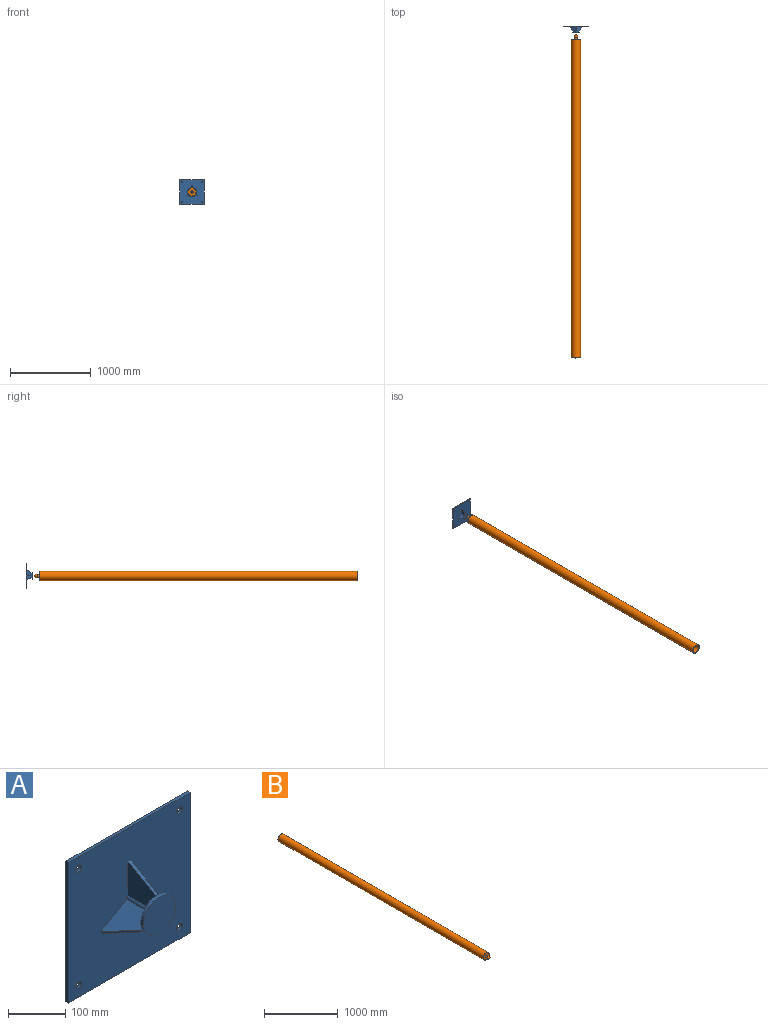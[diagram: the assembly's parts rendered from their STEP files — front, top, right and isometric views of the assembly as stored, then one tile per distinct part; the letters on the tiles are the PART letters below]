
ASSEMBLY  parts=2 mates=2
PART A: 30 faces, bbox 300x80.6x300 mm
  f0: plane 5.63x3.41mm, normal (0,-1,0), area 1.2mm2, adj f2,f23,f24,f27
  f1: plane 6.35x0.27mm, normal (0,-1,0), area 1.2mm2, adj f7,f19,f20,f27
  f2: plane 67.95x64.65mm, normal (0.5,0,0.87), area 3691.5mm2, adj f0,f16,f18,f24,f25
  f3: plane 5.63x3.41mm, normal (0,-1,0), area 1.2mm2, adj f5,f21,f22,f27
  f4: cylinder r=6.35mm len=67.95mm, axis (0,1,0), area 451.8mm2, adj f5,f16,f23,f29
  f5: plane 67.95x64.65mm, normal (0.5,0,-0.87), area 3691.5mm2, adj f3,f4,f16,f22,f29
  f6: cylinder r=6.35mm len=67.95mm, axis (0,1,0), area 451.8mm2, adj f7,f16,f21,f26
  f7: plane 74.65x67.95mm, normal (-1,0,0), area 3691.5mm2, adj f1,f6,f16,f20,f26
  f8: plane 300x6.35mm, normal (0,0,1), area 1905mm2, adj f9,f15,f16,f17
  f9: plane 300x6.35mm, normal (-1,0,0), area 1905mm2, adj f8,f10,f16,f17
  f10: plane 300x6.35mm, normal (0,0,-1), area 1905mm2, adj f9,f15,f16,f17
  f11: cylinder r=7.14mm len=14.29mm, axis (0,1,0), area 285mm2, adj f16,f17
  f12: cylinder r=7.14mm len=14.29mm, axis (0,1,0), area 285mm2, adj f16,f17
  f13: cylinder r=7.14mm len=14.29mm, axis (0,1,0), area 285mm2, adj f16,f17
  f14: cylinder r=7.14mm len=14.29mm, axis (0,1,0), area 285mm2, adj f16,f17
  f15: plane 300x6.35mm, normal (1,0,0), area 1905mm2, adj f8,f10,f16,f17
  f16: plane 300x300mm, normal (0,-1,0), area 87820.9mm2, adj f2,f4,f5,f6,f7,f8,f9,f10
  f17: plane 300x300mm, normal (0,1,0), area 89358.7mm2, adj f8,f9,f10,f11,f12,f13,f14,f15
  f18: cylinder r=6.35mm len=67.95mm, axis (0,1,0), area 451.8mm2, adj f2,f16,f19,f25
  f19: plane 74.65x67.95mm, normal (1,0,0), area 3691.5mm2, adj f1,f16,f18,f20,f25
  f20: plane 67.95x40.64mm, normal (0,-0.51,0.86), area 502.7mm2, adj f1,f7,f16,f19
  f21: plane 67.95x64.65mm, normal (-0.5,0,0.87), area 3691.5mm2, adj f3,f6,f16,f22,f26
  f22: plane 67.95x38.37mm, normal (-0.74,-0.51,-0.43), area 502.7mm2, adj f3,f5,f16,f21
  f23: plane 67.95x64.65mm, normal (-0.5,0,-0.87), area 3691.5mm2, adj f0,f4,f16,f24,f29
  f24: plane 67.95x38.37mm, normal (0.74,-0.51,-0.43), area 502.7mm2, adj f0,f2,f16,f23
  f25: plane 56.11x36.2mm, normal (0,1,0), area 1369.8mm2, adj f2,f18,f19,f27
  f26: plane 56.11x36.2mm, normal (0,1,0), area 1369.8mm2, adj f6,f7,f21,f27
  f27: cylinder r=39.37mm len=78.74mm, axis (0,1,0), area 1570.8mm2, adj f0,f1,f3,f25,f26,f28,f29
  f28: plane 78.74x78.74mm, normal (0,-1,0), area 4869.5mm2, adj f27
  f29: plane 64.79x33.87mm, normal (0,1,0), area 1369.8mm2, adj f4,f5,f23,f27
PART B: 7 faces, bbox 114.3x4011x114.3 mm
  f0: cylinder r=50.8mm len=3943.35mm, axis (0,1,0), area 1258661.4mm2, adj f2,f3
  f1: cylinder r=57.15mm len=3949.7mm, axis (0,1,0), area 1418274.2mm2, adj f2,f4
  f2: plane 114.3x114.3mm, normal (0,1,0), area 2153.5mm2, adj f0,f1
  f3: plane 101.6x101.6mm, normal (0,1,0), area 8107.3mm2, adj f0
  f4: plane 114.3x114.3mm, normal (0,-1,0), area 9754.1mm2, adj f1,f6
  f5: sphere r=20mm, area 4454.8mm2, adj f6
  f6: cylinder r=12.7mm len=25.82mm, axis (0,-1,0), area 2060.7mm2, adj f4,f5
PLACE A t=(-692.63,-15.51,310.29)mm fixed
PLACE B rot(axis=(-0.58,0,-0.81),180deg) t=(-635.22,-4134.76,307.13)mm
MATE cylindrical B.f0 <-> A.f4  axis (0,-1,0) through (-635.22,-4134.76,307.13)mm
MATE planar B.f1 <-> A.f4  axis (0,1,0) through (-635.22,-185.06,307.13)mm
